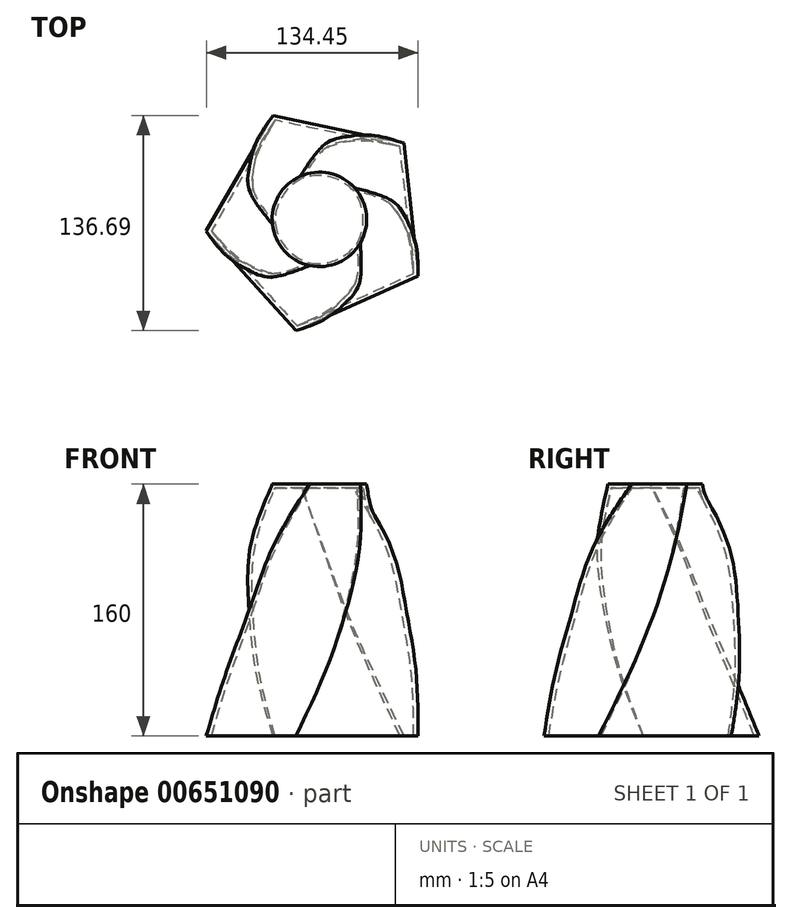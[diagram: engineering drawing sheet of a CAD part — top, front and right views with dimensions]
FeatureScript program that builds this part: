
annotation { "Feature Type Name" : "Feature", "Feature Type Description" : "" }
export const myFeature = defineFeature(function(context is Context, id is Id, definition is map)
    precondition{}
    {
        {
            var Q0;
            Q0=qCreatedBy(makeId("Top.planeOp"),FACE);
            var sketch = newSketch(context, id + "F0", { "sketchPlane" : qUnion([Q0])});
            skCircle(sketch, "E0.cCircle", {"center": v(0, 0) * mm, "radius": 58.46 * mm, "construction": true});
            skLineSegment(sketch, "E0.0", {"start": v(53.7, 48.35) * mm, "end": v(62.58, -36.13) * mm});
            skLineSegment(sketch, "E0.1", {"start": v(62.58, -36.13) * mm, "end": v(-15.02, -70.68) * mm});
            skLineSegment(sketch, "E0.2", {"start": v(-15.02, -70.68) * mm, "end": v(-71.86, -7.55) * mm});
            skLineSegment(sketch, "E0.3", {"start": v(-71.86, -7.55) * mm, "end": v(-29.4, 66.01) * mm});
            skLineSegment(sketch, "E0.4", {"start": v(-29.4, 66.01) * mm, "end": v(53.7, 48.35) * mm});
            skPoint(sketch, "E0.0.midPoint", {"position": v(58.14, 6.11) * mm});
            skSolve(sketch);
        }
        {
            var Q0;
            Q0=qCreatedBy(makeId("Top.planeOp"),FACE);
            cPlane(context, id + "F1", {"entities" : qUnion([Q0]), "cplaneType" : CPlaneType.OFFSET, "offset" : 40 * mm, "width" : 150 * mm, "height" : 150 * mm});
        }
        {
            var Q0;
            Q0=qCreatedBy(id+"F1.planeOp",FACE);
            var sketch = newSketch(context, id + "F2", { "sketchPlane" : qUnion([Q0])});
            skCircle(sketch, "E1.cCircle", {"center": v(0, 0) * mm, "radius": 51.43 * mm, "construction": true});
            skLineSegment(sketch, "E1.0", {"start": v(-40, 49.4) * mm, "end": v(34.62, 53.31) * mm});
            skLineSegment(sketch, "E1.1", {"start": v(34.62, 53.31) * mm, "end": v(61.4, -16.45) * mm});
            skLineSegment(sketch, "E1.2", {"start": v(61.4, -16.45) * mm, "end": v(3.33, -63.48) * mm});
            skLineSegment(sketch, "E1.3", {"start": v(3.33, -63.48) * mm, "end": v(-59.35, -22.78) * mm});
            skLineSegment(sketch, "E1.4", {"start": v(-59.35, -22.78) * mm, "end": v(-40, 49.4) * mm});
            skPoint(sketch, "E1.0.midPoint", {"position": v(-2.7, 51.36) * mm});
            skSolve(sketch);
        }
        {
            var Q0;
            Q0=qCreatedBy(id+"F1.planeOp",FACE);
            cPlane(context, id + "F3", {"entities" : qUnion([Q0]), "cplaneType" : CPlaneType.OFFSET, "offset" : 40 * mm, "width" : 150 * mm, "height" : 150 * mm});
        }
        {
            var Q0;
            Q0=qCreatedBy(id+"F3.planeOp",FACE);
            var sketch = newSketch(context, id + "F4", { "sketchPlane" : qUnion([Q0])});
            skCircle(sketch, "E2.cCircle", {"center": v(0, 0) * mm, "radius": 44.72 * mm, "construction": true});
            skLineSegment(sketch, "E2.0", {"start": v(-44.72, 32.5) * mm, "end": v(17.08, 52.57) * mm});
            skLineSegment(sketch, "E2.1", {"start": v(17.08, 52.57) * mm, "end": v(55.28, 0) * mm});
            skLineSegment(sketch, "E2.2", {"start": v(55.28, 0) * mm, "end": v(17.08, -52.57) * mm});
            skLineSegment(sketch, "E2.3", {"start": v(17.08, -52.57) * mm, "end": v(-44.72, -32.5) * mm});
            skLineSegment(sketch, "E2.4", {"start": v(-44.72, -32.5) * mm, "end": v(-44.72, 32.5) * mm});
            skPoint(sketch, "E2.0.midPoint", {"position": v(-13.82, 42.53) * mm});
            skSolve(sketch);
        }
        {
            var Q0;
            Q0=qCreatedBy(id+"F3.planeOp",FACE);
            cPlane(context, id + "F5", {"entities" : qUnion([Q0]), "cplaneType" : CPlaneType.OFFSET, "offset" : 40 * mm, "width" : 150 * mm, "height" : 150 * mm});
        }
        {
            var Q0;
            Q0=qCreatedBy(id+"F5.planeOp",FACE);
            var sketch = newSketch(context, id + "F6", { "sketchPlane" : qUnion([Q0])});
            skCircle(sketch, "E3.cCircle", {"center": v(0, 0) * mm, "radius": 38.01 * mm, "construction": true});
            skLineSegment(sketch, "E3.0", {"start": v(-43.87, 16.84) * mm, "end": v(2.46, 46.92) * mm});
            skLineSegment(sketch, "E3.1", {"start": v(2.46, 46.92) * mm, "end": v(45.39, 12.16) * mm});
            skLineSegment(sketch, "E3.2", {"start": v(45.39, 12.16) * mm, "end": v(25.6, -39.4) * mm});
            skLineSegment(sketch, "E3.3", {"start": v(25.6, -39.4) * mm, "end": v(-29.57, -36.52) * mm});
            skLineSegment(sketch, "E3.4", {"start": v(-29.57, -36.52) * mm, "end": v(-43.87, 16.84) * mm});
            skPoint(sketch, "E3.0.midPoint", {"position": v(-20.7, 31.88) * mm});
            skSolve(sketch);
        }
        {
            var Q0;
            Q0=qCreatedBy(id+"F5.planeOp",FACE);
            cPlane(context, id + "F7", {"entities" : qUnion([Q0]), "cplaneType" : CPlaneType.OFFSET, "offset" : 40 * mm, "width" : 150 * mm, "height" : 150 * mm});
        }
        {
            var Q0;
            Q0=qCreatedBy(id+"F7.planeOp",FACE);
            var sketch = newSketch(context, id + "F8", { "sketchPlane" : qUnion([Q0])});
            skCircle(sketch, "E4", {"center": v(0, 0) * mm, "radius": 30 * mm});
            skPoint(sketch, "E5", {"position": v(25.98, -15) * mm});
            skLineSegment(sketch, "E6", {"start": v(0, 0) * mm, "end": v(0, -30) * mm, "construction": true});
            skLineSegment(sketch, "E7", {"start": v(0, 0) * mm, "end": v(25.98, -15) * mm, "construction": true});
            skSolve(sketch);
        }
        {
            var Q0;
            Q0=makeQuery(id+"F0.imprint","IMPRINT",FACE,{"disambiguationData":[TD([[makeQuery(id+"F0.imprint","IMPRINT",EDGE,{"derivedFrom":sQuery(id+"F0.wireOp",EDGE,"E0.0")}),-1.0]])]});
            var Q1;
            Q1=makeQuery(id+"F2.imprint","IMPRINT",FACE,{"disambiguationData":[TD([[makeQuery(id+"F2.imprint","IMPRINT",EDGE,{"derivedFrom":sQuery(id+"F2.wireOp",EDGE,"E1.0")}),-1.0]])]});
            var Q2;
            Q2=makeQuery(id+"F4.imprint","IMPRINT",FACE,{"disambiguationData":[TD([[makeQuery(id+"F4.imprint","IMPRINT",EDGE,{"derivedFrom":sQuery(id+"F4.wireOp",EDGE,"E2.0")}),-1.0]])]});
            var Q3;
            Q3=makeQuery(id+"F6.imprint","IMPRINT",FACE,{"disambiguationData":[TD([[makeQuery(id+"F6.imprint","IMPRINT",EDGE,{"derivedFrom":sQuery(id+"F6.wireOp",EDGE,"E3.0")}),-1.0]])]});
            var Q4;
            Q4=makeQuery(id+"F8.imprint","IMPRINT",FACE,{"disambiguationData":[TD([[makeQuery(id+"F8.imprint","IMPRINT",EDGE,{"derivedFrom":sQuery(id+"F8.wireOp",EDGE,"E4")}),1.0]])]});
            var Q5;
            Q5=sQuery(id+"F0.wireOp",VERTEX,"E0.2.start");
            var Q6;
            Q6=sQuery(id+"F2.wireOp",VERTEX,"E1.3.start");
            var Q7;
            Q7=sQuery(id+"F4.wireOp",VERTEX,"E2.3.start");
            var Q8;
            Q8=sQuery(id+"F6.wireOp",VERTEX,"E3.3.start");
            var Q9;
            Q9=sQuery(id+"F8.wireOp",VERTEX,"E5");
            loft(context, id + "F9", {"sheetProfilesArray" : [{ "sheetProfileEntities" : qUnion([Q0]) }, { "sheetProfileEntities" : qUnion([Q1]) }, { "sheetProfileEntities" : qUnion([Q2]) }, { "sheetProfileEntities" : qUnion([Q3]) }, { "sheetProfileEntities" : qUnion([Q4]) }], "matchConnections" : true, "connections" : [{ "connectionEntities" : qUnion([Q5, Q6, Q7, Q8, Q9]), "connectionEdgeQueries" : qUnion([]), "connectionEdgeParameters" : [] }]});
        }
        {
            var Q0;
            Q0=makeQuery(id+"F9.opLoft","CAP_FACE",FACE,{"disambiguationData":[OSD([makeQuery(id+"F0.imprint","IMPRINT",FACE,{"disambiguationData":[TD([[makeQuery(id+"F0.imprint","IMPRINT",EDGE,{"derivedFrom":sQuery(id+"F0.wireOp",EDGE,"E0.0")}),-1.0]])]})])],"isStart":true});
            shell(context, id + "F10", {"entities" : qUnion([Q0]), "thickness" : 2.5 * mm});
        }
    });
